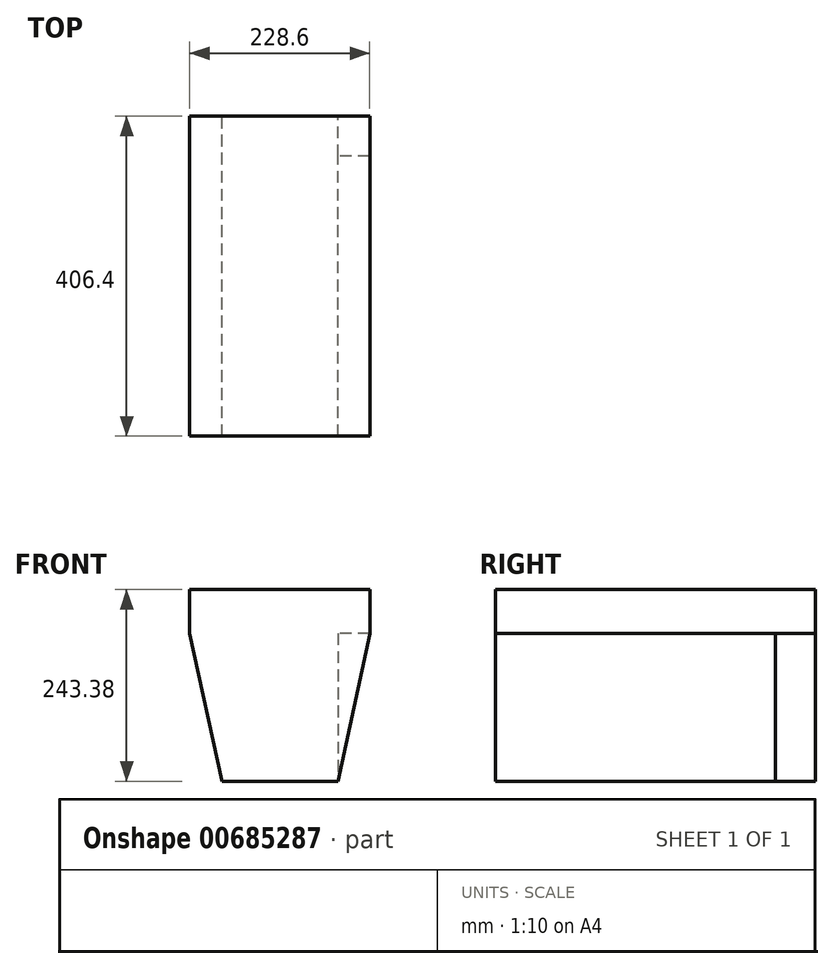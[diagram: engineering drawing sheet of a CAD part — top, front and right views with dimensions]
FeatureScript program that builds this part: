
annotation { "Feature Type Name" : "Feature", "Feature Type Description" : "" }
export const myFeature = defineFeature(function(context is Context, id is Id, definition is map)
    precondition{}
    {
        {
            var Q0;
            Q0=qCreatedBy(makeId("Front.planeOp"),FACE);
            var sketch = newSketch(context, id + "F0", { "sketchPlane" : qUnion([Q0])});
            skLineSegment(sketch, "E0", {"start": v(-114.9, 107.4) * mm, "end": v(113.7, 107.4) * mm});
            skLineSegment(sketch, "E1", {"start": v(113.7, 107.4) * mm, "end": v(113.7, 52.07) * mm});
            skLineSegment(sketch, "E2", {"start": v(113.7, 52.07) * mm, "end": v(73.05, -135.99) * mm});
            skLineSegment(sketch, "E3", {"start": v(73.05, -135.99) * mm, "end": v(-74.27, -135.99) * mm});
            skLineSegment(sketch, "E4", {"start": v(-74.27, -135.99) * mm, "end": v(-114.9, 52.07) * mm});
            skLineSegment(sketch, "E5", {"start": v(-114.9, 52.07) * mm, "end": v(-114.9, 107.4) * mm});
            skSolve(sketch);
        }
        {
            var Q0;
            Q0 = qSketchRegion(id + "F0", true);
            extrude(context, id + "F1", {"entities" : qUnion([Q0]), "depth" : 406.4 * mm, "offsetDistance" : 25.4 * mm});
        }
        {
            var Q0;
            Q0=makeQuery(id+"F1.opExtrude","CAP_FACE",FACE,{"disambiguationData":[OSD([sQuery(id+"F0.wireOp",EDGE,"E0"),sQuery(id+"F0.wireOp",EDGE,"E1"),sQuery(id+"F0.wireOp",EDGE,"E2"),sQuery(id+"F0.wireOp",EDGE,"E3"),sQuery(id+"F0.wireOp",EDGE,"E4"),sQuery(id+"F0.wireOp",EDGE,"E5")])],"isStart":true});
            var sketch = newSketch(context, id + "F2", { "sketchPlane" : qUnion([Q0])});
            skLineSegment(sketch, "E6", {"start": v(-113.7, 52.07) * mm, "end": v(-73.05, 52.07) * mm});
            skLineSegment(sketch, "E7", {"start": v(-73.05, 52.07) * mm, "end": v(-73.05, -135.99) * mm});
            skLineSegment(sketch, "E8", {"start": v(-73.05, -135.99) * mm, "end": v(-113.7, 52.07) * mm});
            skSolve(sketch);
        }
        {
            var Q0;
            Q0 = qSketchRegion(id + "F2", true);
            extrude(context, id + "F3", {"entities" : qUnion([Q0]), "operationType" : NewBodyOperationType.REMOVE, "oppositeDirection" : true, "depth" : 50.8 * mm, "offsetDistance" : 25.4 * mm});
        }
    });
